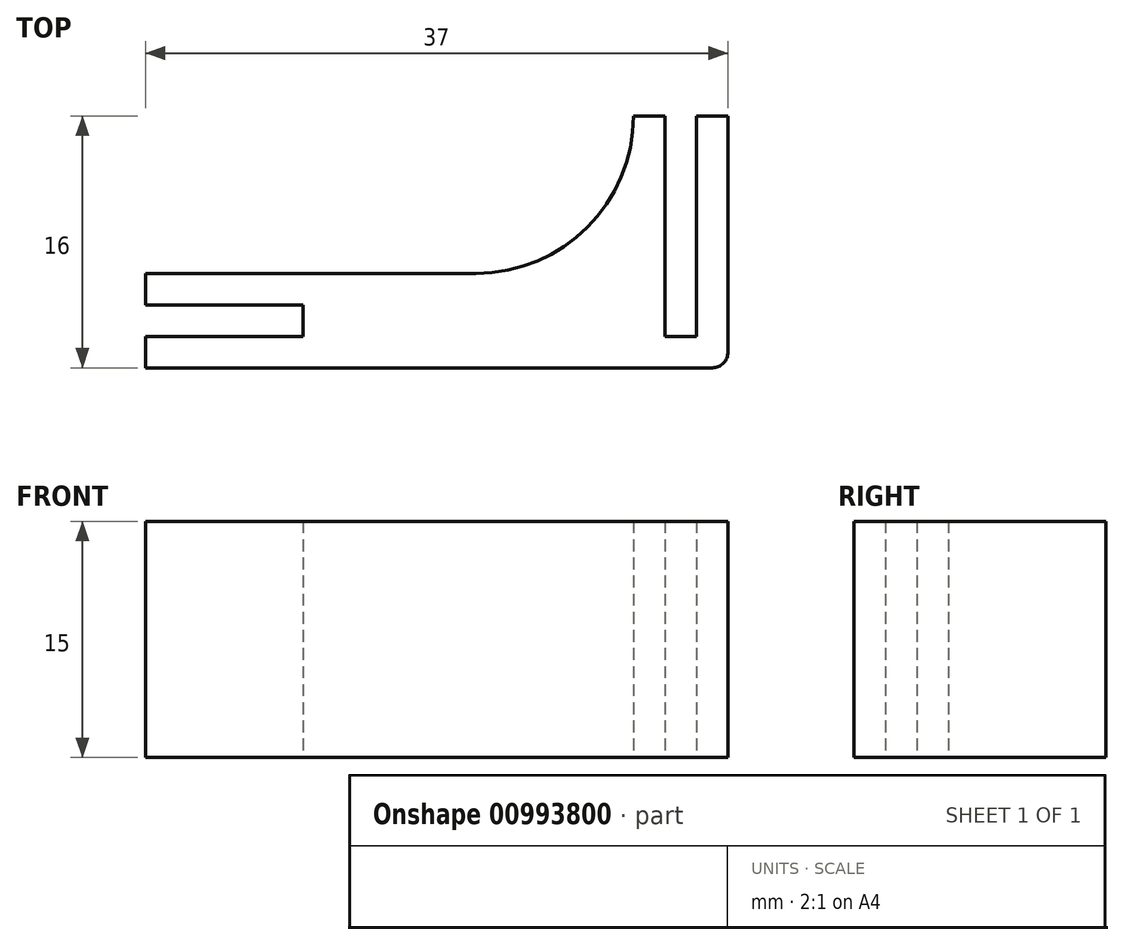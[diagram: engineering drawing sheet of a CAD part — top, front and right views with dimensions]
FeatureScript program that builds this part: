
annotation { "Feature Type Name" : "Feature", "Feature Type Description" : "" }
export const myFeature = defineFeature(function(context is Context, id is Id, definition is map)
    precondition{}
    {
        {
            var Q0;
            Q0=qCreatedBy(makeId("Top.planeOp"),FACE);
            var sketch = newSketch(context, id + "F0", { "sketchPlane" : qUnion([Q0])});
            skLineSegment(sketch, "E0", {"start": v(-9.75, 8.3) * mm, "end": v(-9.75, 18.3) * mm});
            skLineSegment(sketch, "E1", {"start": v(-9.75, 18.3) * mm, "end": v(-7.75, 18.3) * mm});
            skLineSegment(sketch, "E2", {"start": v(-7.75, 18.3) * mm, "end": v(-7.75, 4.3) * mm});
            skLineSegment(sketch, "E3", {"start": v(-7.75, 4.3) * mm, "end": v(-5.75, 4.3) * mm});
            skLineSegment(sketch, "E4", {"start": v(-5.75, 4.3) * mm, "end": v(-5.75, 18.3) * mm});
            skLineSegment(sketch, "E5", {"start": v(-5.75, 18.3) * mm, "end": v(-3.75, 18.3) * mm});
            skLineSegment(sketch, "E6", {"start": v(-3.75, 18.3) * mm, "end": v(-3.75, 2.3) * mm});
            skLineSegment(sketch, "E7", {"start": v(-3.75, 2.3) * mm, "end": v(-40.75, 2.3) * mm});
            skLineSegment(sketch, "E8", {"start": v(-40.75, 2.3) * mm, "end": v(-40.75, 4.3) * mm});
            skLineSegment(sketch, "E9", {"start": v(-40.75, 4.3) * mm, "end": v(-30.75, 4.3) * mm});
            skLineSegment(sketch, "E10", {"start": v(-30.75, 4.3) * mm, "end": v(-30.75, 6.3) * mm});
            skLineSegment(sketch, "E11", {"start": v(-30.75, 6.3) * mm, "end": v(-40.75, 6.3) * mm});
            skLineSegment(sketch, "E12", {"start": v(-40.75, 6.3) * mm, "end": v(-40.75, 8.3) * mm});
            skLineSegment(sketch, "E13", {"start": v(-9.75, 8.3) * mm, "end": v(-40.75, 8.3) * mm});
            skSolve(sketch);
        }
        {
            var Q0;
            Q0=makeQuery(id+"F0.imprint","IMPRINT",FACE,{"disambiguationData":[TD([[makeQuery(id+"F0.imprint","IMPRINT",EDGE,{"derivedFrom":sQuery(id+"F0.wireOp",EDGE,"E0")}),-1.0]])]});
            extrude(context, id + "F1", {"entities" : qUnion([Q0]), "depth" : 15 * mm, "offsetDistance" : 25 * mm, "symmetric" : true});
        }
        {
            var Q0;
            Q0=makeQuery(id+"F1.opExtrude","SWEPT_EDGE",EDGE,{"disambiguationData":[OSD([sQuery(id+"F0.wireOp",EDGE,"E0"),sQuery(id+"F0.wireOp",EDGE,"E13")])]});
            fillet(context, id + "F2", {"entities" : qUnion([Q0]), "tangentPropagation" : true, "radius" : 10 * mm, "defaultsChanged" : true, "vertexSettings" : [], "allowEdgeOverflow" : false});
        }
        {
            var Q0;
            Q0=makeQuery(id+"F1.opExtrude","SWEPT_EDGE",EDGE,{"disambiguationData":[OSD([sQuery(id+"F0.wireOp",EDGE,"E6"),sQuery(id+"F0.wireOp",EDGE,"E7")])]});
            fillet(context, id + "F3", {"entities" : qUnion([Q0]), "tangentPropagation" : true, "radius" : 1 * mm, "defaultsChanged" : true, "vertexSettings" : [], "allowEdgeOverflow" : false});
        }
    });
